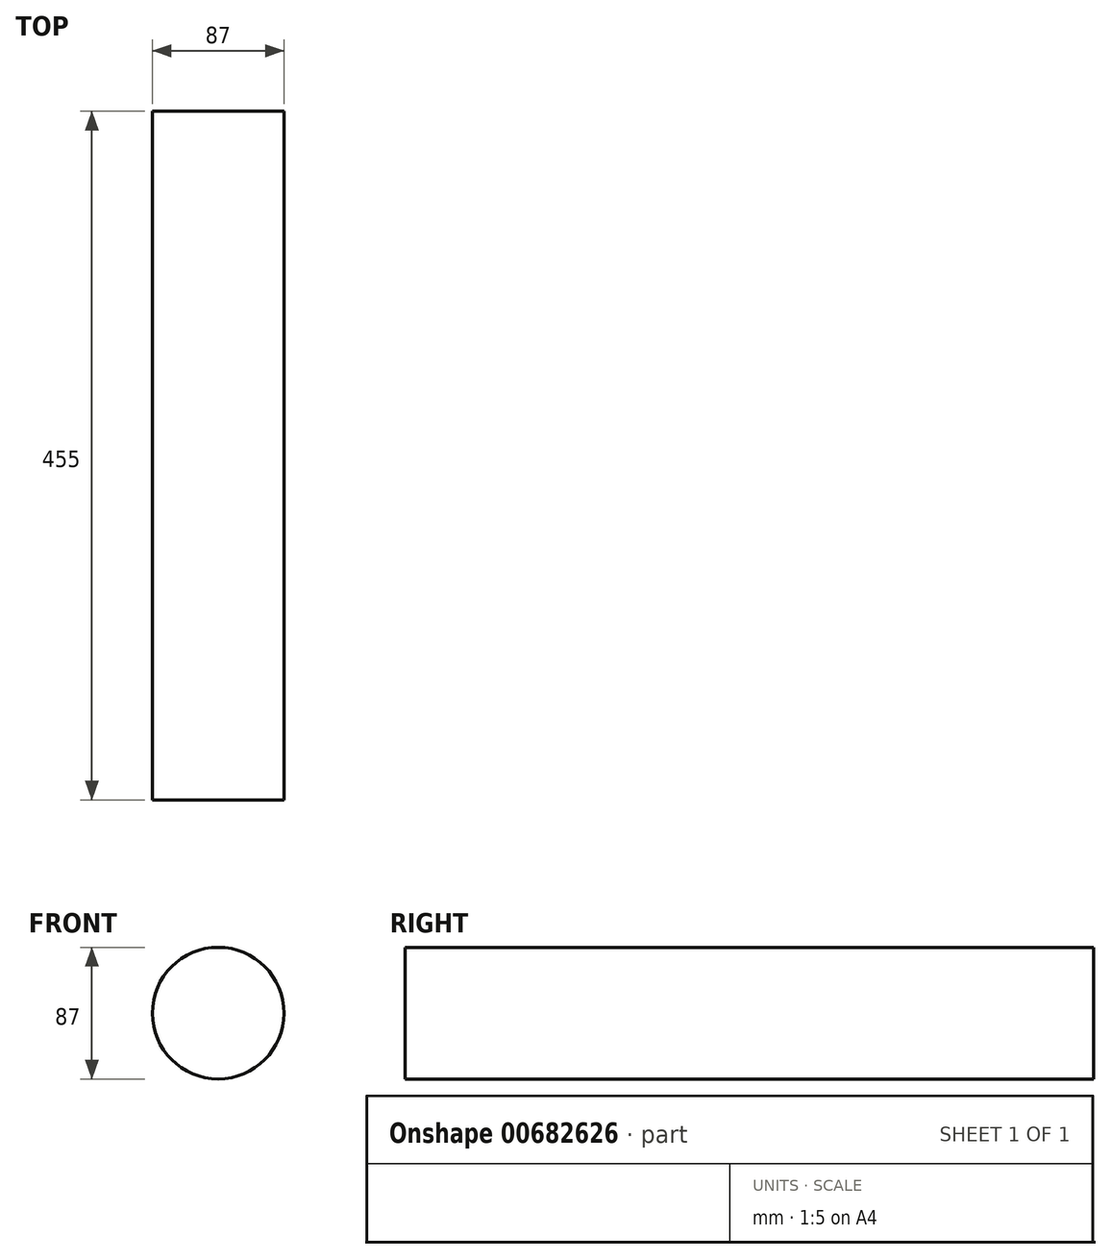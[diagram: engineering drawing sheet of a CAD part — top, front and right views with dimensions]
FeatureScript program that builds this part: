
annotation { "Feature Type Name" : "Feature", "Feature Type Description" : "" }
export const myFeature = defineFeature(function(context is Context, id is Id, definition is map)
    precondition{}
    {
        {
            var Q0;
            Q0=qCreatedBy(makeId("Front.planeOp"),FACE);
            var sketch = newSketch(context, id + "F0", { "sketchPlane" : qUnion([Q0])});
            skCircle(sketch, "E0", {"center": v(0, 0) * mm, "radius": 43.5 * mm});
            skSolve(sketch);
        }
        {
            var Q0;
            Q0=makeQuery(id+"F0.imprint","IMPRINT",FACE,{"disambiguationData":[TD([[makeQuery(id+"F0.imprint","IMPRINT",EDGE,{"derivedFrom":sQuery(id+"F0.wireOp",EDGE,"E0")}),1.0]])]});
            extrude(context, id + "F1", {"entities" : qUnion([Q0]), "depth" : 455 * mm, "offsetDistance" : 25 * mm});
        }
    });
